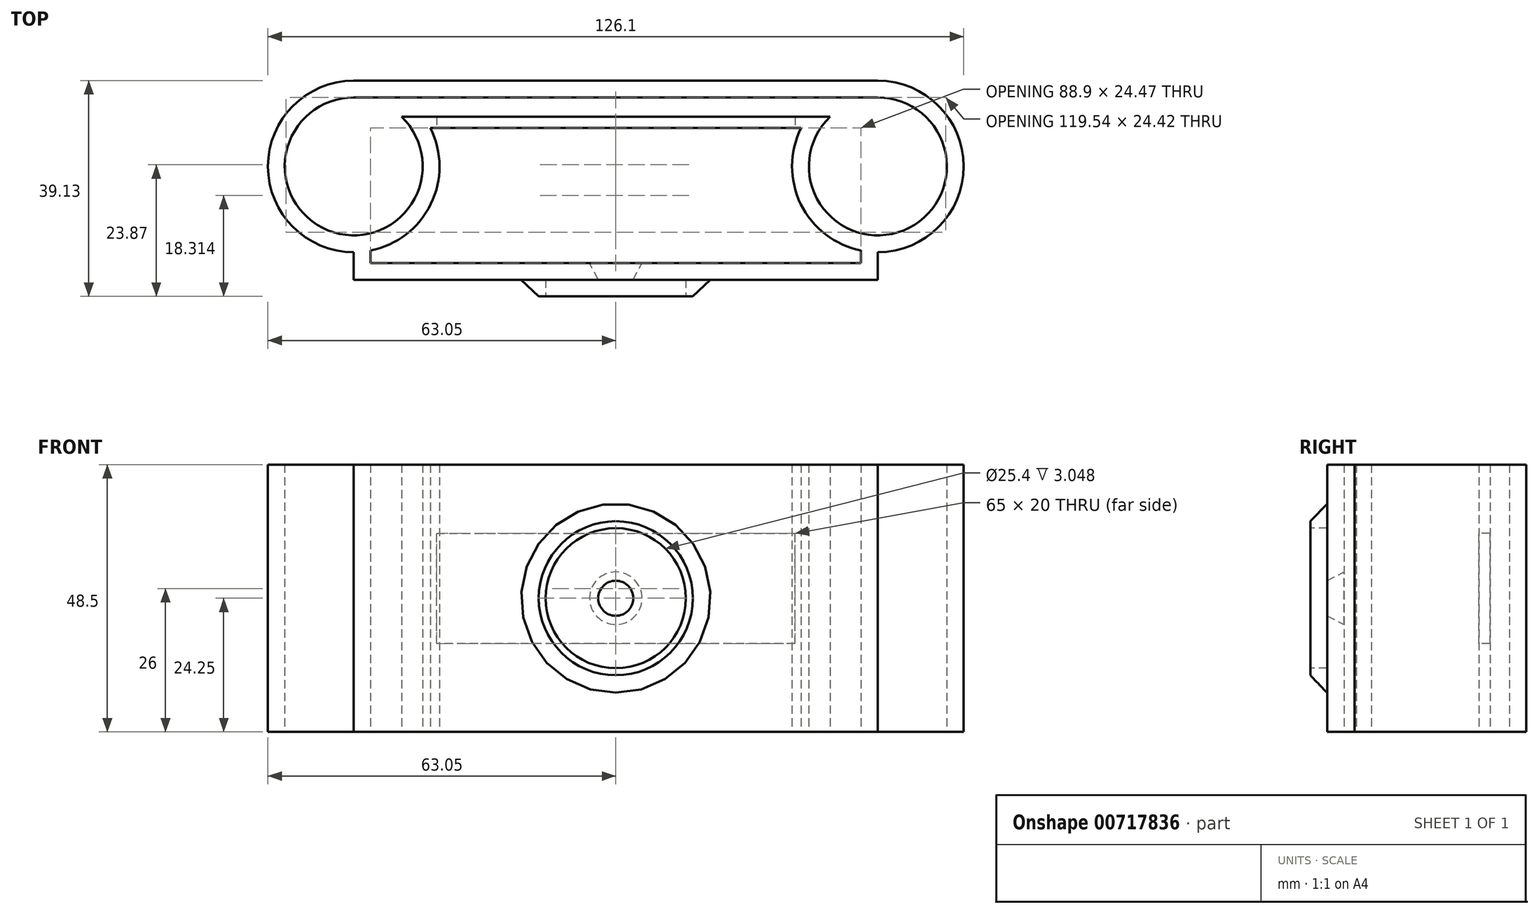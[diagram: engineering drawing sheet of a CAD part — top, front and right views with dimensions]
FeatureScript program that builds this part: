
annotation { "Feature Type Name" : "Feature", "Feature Type Description" : "" }
export const myFeature = defineFeature(function(context is Context, id is Id, definition is map)
    precondition{}
    {
        {
            var Q0;
            Q0=qCreatedBy(makeId("Top.planeOp"),FACE);
            var sketch = newSketch(context, id + "F0", { "sketchPlane" : qUnion([Q0])});
            skLineSegment(sketch, "E0.bottom", {"start": v(44.45, 15) * mm, "end": v(38.25, 15) * mm});
            skLineSegment(sketch, "E0.top", {"start": v(44.45, -15) * mm, "end": v(-44.45, -15) * mm});
            skLineSegment(sketch, "E0.left", {"start": v(44.45, 15) * mm, "end": v(44.45, -15) * mm});
            skLineSegment(sketch, "E0.right", {"start": v(-44.45, 15) * mm, "end": v(-44.45, -15) * mm});
            skPoint(sketch, "E0.middle", {"position": v(0, 0) * mm});
            skLineSegment(sketch, "E1.0", {"start": v(47.5, 18.05) * mm, "end": v(-47.5, 18.05) * mm});
            skLineSegment(sketch, "E1.1", {"start": v(47.5, 18.05) * mm, "end": v(47.5, 15) * mm});
            skLineSegment(sketch, "E1.2", {"start": v(47.5, -18.05) * mm, "end": v(-47.5, -18.05) * mm});
            skLineSegment(sketch, "E1.3", {"start": v(-47.5, 18.05) * mm, "end": v(-47.5, -18.05) * mm});
            skLineSegment(sketch, "E2", {"start": v(38.25, 15) * mm, "end": v(-44.45, 15) * mm});
            skArc(sketch, "E3", {"start": v(34.82, 11.5) * mm, "mid": v(58.6, -8.39) * mm, "end": v(38.25, 15) * mm});
            skLineSegment(sketch, "E4", {"start": v(47.5, 15) * mm, "end": v(47.5, -18.05) * mm});
            skArc(sketch, "E5", {"start": v(38.82, 11.5) * mm, "mid": v(52.18, -9.1) * mm, "end": v(47.5, 15) * mm});
            skLineSegment(sketch, "E6", {"start": v(38.82, 11.5) * mm, "end": v(34.82, 11.5) * mm});
            skLineSegment(sketch, "E7", {"start": v(47.5, 15) * mm, "end": v(44.45, 15) * mm});
            skArc(sketch, "E8", {"start": v(-38.25, 15) * mm, "mid": v(-58.6, -8.39) * mm, "end": v(-34.82, 11.5) * mm});
            skArc(sketch, "E9", {"start": v(-47.5, 15) * mm, "mid": v(-52.18, -9.1) * mm, "end": v(-38.82, 11.5) * mm});
            skLineSegment(sketch, "E10", {"start": v(-38.82, 11.5) * mm, "end": v(-34.82, 11.5) * mm});
            skLineSegment(sketch, "E11", {"start": v(-47.5, 15) * mm, "end": v(-44.45, 15) * mm});
            skLineSegment(sketch, "E12", {"start": v(-34.82, 11.5) * mm, "end": v(34.82, 11.5) * mm});
            skLineSegment(sketch, "E13", {"start": v(34.82, 9.46) * mm, "end": v(-34.82, 9.47) * mm});
            skLineSegment(sketch, "E14", {"start": v(-34.82, 9.47) * mm, "end": v(-34.82, 11.5) * mm});
            skLineSegment(sketch, "E15", {"start": v(34.82, 11.5) * mm, "end": v(34.82, 9.46) * mm});
            skSolve(sketch);
        }
        {
            var Q0;
            Q0=qSketchRegion(id+"F0",true);
            var Q1;
            {var subQ0=sQuery(id+"F0.wireOp",EDGE,"E10");Q1=makeQuery(id+"F0.imprint","IMPRINT",FACE,{"disambiguationData":[TD([[makeQuery(id+"F0.imprint","IMPRINT",EDGE,{"derivedFrom":subQ0}),-1.0]])]});}
            var Q2;
            {var subQ0=sQuery(id+"F0.wireOp",EDGE,"E12");Q2=makeQuery(id+"F0.imprint","IMPRINT",FACE,{"disambiguationData":[TD([[makeQuery(id+"F0.imprint","IMPRINT",EDGE,{"derivedFrom":subQ0}),-1.0]])]});}
            var Q3;
            {var subQ0=sQuery(id+"F0.wireOp",EDGE,"E14");Q3=makeQuery(id+"F0.imprint","IMPRINT",FACE,{"disambiguationData":[TD([[makeQuery(id+"F0.imprint","IMPRINT",EDGE,{"derivedFrom":subQ0}),-1.0]])]});}
            var Q4;
            {var subQ0=sQuery(id+"F0.wireOp",EDGE,"E15");Q4=makeQuery(id+"F0.imprint","IMPRINT",FACE,{"disambiguationData":[TD([[makeQuery(id+"F0.imprint","IMPRINT",EDGE,{"derivedFrom":subQ0}),-1.0]])]});}
            var Q5;
            {var subQ0=sQuery(id+"F0.wireOp",EDGE,"E6");Q5=makeQuery(id+"F0.imprint","IMPRINT",FACE,{"disambiguationData":[TD([[makeQuery(id+"F0.imprint","IMPRINT",EDGE,{"derivedFrom":subQ0}),1.0]])]});}
            extrude(context, id + "F1", {"entities" : qUnion([Q0, Q1, Q2, Q3, Q4, Q5]), "endBound" : BoundingType.SYMMETRIC, "depth" : 48.5 * mm, "offsetDistance" : 25.4 * mm});
        }
        {
            var Q0;
            Q0=qCreatedBy(makeId("Front.planeOp"),FACE);
            cPlane(context, id + "F2", {"entities" : qUnion([Q0]), "cplaneType" : CPlaneType.OFFSET, "offset" : 18.05 * mm, "width" : 152.4 * mm, "height" : 152.4 * mm});
        }
        {
            var Q0;
            Q0=qCreatedBy(makeId("Front.planeOp"),FACE);
            cPlane(context, id + "F3", {"entities" : qUnion([Q0]), "cplaneType" : CPlaneType.OFFSET, "offset" : 15 * mm, "width" : 152.4 * mm, "height" : 152.4 * mm});
        }
        {
            var Q0;
            Q0=qCreatedBy(id+"F2.planeOp",FACE);
            var sketch = newSketch(context, id + "F4", { "sketchPlane" : qUnion([Q0])});
            skCircle(sketch, "E16", {"center": v(0, 0) * mm, "radius": 3.18 * mm});
            skSolve(sketch);
        }
        {
            var Q0;
            Q0=qCreatedBy(id+"F3.planeOp",FACE);
            var sketch = newSketch(context, id + "F5", { "sketchPlane" : qUnion([Q0])});
            skCircle(sketch, "E17", {"center": v(0, 0) * mm, "radius": 4.76 * mm});
            skSolve(sketch);
        }
        {
            var Q1;
            Q1=qSketchRegion(id+"F4",true);
            var Q2;
            Q2=qSketchRegion(id+"F5",true);
            loft(context, id + "F6", {"operationType" : NewBodyOperationType.REMOVE, "sheetProfilesArray" : [{ "sheetProfileEntities" : qUnion([Q1]) }, { "sheetProfileEntities" : qUnion([Q2]) }]});
        }
        {
            var Q0;
            Q0=qCreatedBy(makeId("Front.planeOp"),FACE);
            cPlane(context, id + "F7", {"entities" : qUnion([Q0]), "cplaneType" : CPlaneType.OFFSET, "offset" : 21.08 * mm, "width" : 152.4 * mm, "height" : 152.4 * mm});
        }
        {
            var Q0;
            Q0=qCreatedBy(id+"F2.planeOp",FACE);
            var sketch = newSketch(context, id + "F8", { "sketchPlane" : qUnion([Q0])});
            skCircle(sketch, "E18", {"center": v(0, 0) * mm, "radius": 17.15 * mm});
            skSolve(sketch);
        }
        {
            var Q0;
            Q0=qCreatedBy(id+"F7.planeOp",FACE);
            var sketch = newSketch(context, id + "F9", { "sketchPlane" : qUnion([Q0])});
            skCircle(sketch, "E19", {"center": v(0, 0) * mm, "radius": 13.97 * mm});
            skSolve(sketch);
        }
        {
            var Q1;
            Q1=qSketchRegion(id+"F8",true);
            var Q2;
            Q2=makeQuery(id+"F9.imprint","IMPRINT",FACE,{"disambiguationData":[TD([[makeQuery(id+"F9.imprint","IMPRINT",EDGE,{"derivedFrom":sQuery(id+"F9.wireOp",EDGE,"E19")}),1.0]])]});
            loft(context, id + "F10", {"operationType" : NewBodyOperationType.ADD, "sheetProfilesArray" : [{ "sheetProfileEntities" : qUnion([Q1]) }, { "sheetProfileEntities" : qUnion([Q2]) }]});
        }
        {
            var Q0;
            Q0=qCreatedBy(id+"F7.planeOp",FACE);
            var sketch = newSketch(context, id + "F11", { "sketchPlane" : qUnion([Q0])});
            skCircle(sketch, "E20", {"center": v(0, 0) * mm, "radius": 12.7 * mm});
            skSolve(sketch);
        }
        {
            var Q0;
            Q0=qSketchRegion(id+"F11",true);
            extrude(context, id + "F12", {"entities" : qUnion([Q0]), "operationType" : NewBodyOperationType.REMOVE, "oppositeDirection" : true, "depth" : 3.05 * mm, "offsetDistance" : 25.4 * mm});
        }
        {
            var Q0;
            Q0=qCreatedBy(makeId("Front.planeOp"),FACE);
            cPlane(context, id + "F13", {"entities" : qUnion([Q0]), "cplaneType" : CPlaneType.OFFSET, "offset" : 9.46 * mm, "oppositeDirection" : true, "width" : 152.4 * mm, "height" : 152.4 * mm});
        }
        {
            var Q0;
            Q0=qCreatedBy(id+"F13.planeOp",FACE);
            var sketch = newSketch(context, id + "F14", { "sketchPlane" : qUnion([Q0])});
            skPoint(sketch, "E21.middle", {"position": v(0, 0) * mm});
            skLineSegment(sketch, "E22.bottom", {"start": v(32.5, -8.25) * mm, "end": v(-32.5, -8.25) * mm});
            skLineSegment(sketch, "E22.top", {"start": v(32.5, 11.75) * mm, "end": v(-32.5, 11.75) * mm});
            skLineSegment(sketch, "E22.left", {"start": v(32.5, -8.25) * mm, "end": v(32.5, 11.75) * mm});
            skLineSegment(sketch, "E22.right", {"start": v(-32.5, -8.25) * mm, "end": v(-32.5, 11.75) * mm});
            skSolve(sketch);
        }
        {
            var Q0;
            Q0=qSketchRegion(id+"F14",true);
            extrude(context, id + "F15", {"entities" : qUnion([Q0]), "operationType" : NewBodyOperationType.REMOVE, "oppositeDirection" : true, "depth" : 2.03 * mm, "offsetDistance" : 25.4 * mm});
        }
    });
